# Revit family: DSI-HHS10B_2HR_Horizontal-Fire-Curtain_Floor_Door-Systems
name_source: partatom
category: Generic Models
units: mm (PartAtom-declared; Revit-internal decimal feet)

## family parameters
Always vertical = Yes
Can host rebar = No
Cut with Voids When Loaded = No
Part Type = Normal
Room Calculation Point = No
Round Connector Dimension = Use Diameter
Shared = No
Work Plane-Based = No

## types (1)
- DSI-HHS10B_2HR_Horizontal-Fire-Curtain_Floor_Door-Systems
    Bottom Bar = 2mm THK  PRIMED STEEL  BOTTOM BAR
    Cost = 0 $
    Curtain = Curtain
    Curtain Box = 1.2mmTHK PRIMED STEEL
    Curtain Fabric = HS690-SS FABRIC- UL 10B
    Default Elevation = 0' - 0"
    End Plate = 3mmTHK PRIMED STEEL END PLATES AND BRACKETS
    Guide Rail = 2 mm THK PRIMED STEEL GUIDE RAIL
    Keynote = 08 33 44
    Manufacturer = Door Systems
    Model = DSI-HHS10B 2HR Horizontal Curtain Floor
    Motor = INTERNAL, ELECTRIC, TUBULER GEARED CONSTANT SPEED MOTOR
    Open Fire Curtain = Yes
    Power Supply = 120v
    Primed Steel = Primed Steel
    Product Information = https://www.arcat.com
    Schematic Floor = No
    Specifications = https://www.arcat.com
    URL = https://www.doorsysinc.com

## geometry (parser evidence)
native form markers: Sweep x3
no freeform markers — native parametric forms only
